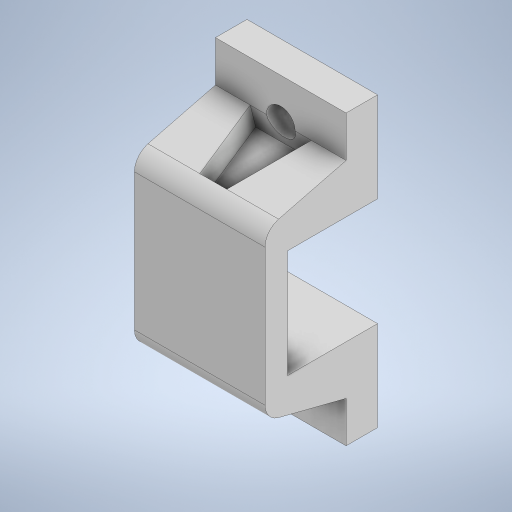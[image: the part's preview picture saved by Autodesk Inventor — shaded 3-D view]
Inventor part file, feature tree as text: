
AUTODESK INVENTOR PART (.ipt)
format: ipt  version: 2024 (Build 280153020, 153B)  size: 305,664 bytes
history: native  units: mm
features: extrude x5, sketch x5
ambient origin geometry x8: Origin, YZ Plane, XZ Plane, XY Plane, X Axis, Y Axis, Z Axis, Center Point
bodies: Solid1 (feature_tree)
feature tree (10):
  extrude  "Extrusion1"  Depth=10.0mm
  extrude  "Extrusion2"  Depth=10.0mm
  extrude  "Extrusion3"  Depth=3.5mm
  extrude  "Extrusion4"  Depth=14.5mm TaperAngle=0.0deg
  extrude  "Extrusion5"  Depth=2.5mm
  sketch  "Sketch1"  dims[d0=12.0mm d1=10.0mm]
  sketch  "Sketch2"  dims[d2=2.5mm d3=10.0mm]
  sketch  "Sketch3"  dims[d4=3.5mm d5=4.56mm]
  sketch  "Sketch4"  dims[d6=2.0mm d7=14.5mm d8=0.0mm]
  sketch  "Sketch5"  dims[d13=1.5mm d14=1.5mm d15=3.4mm d16=3.4mm d17=2.5mm d18=0.0mm d19=3.2mm d20=4.0mm d21=0.0mm d22=3.4mm d23=3.4mm d25=1.5mm d26=1.5mm d27=2.5mm d28=0.0mm d29=3.2mm d30=4.0mm d31=0.0mm]
